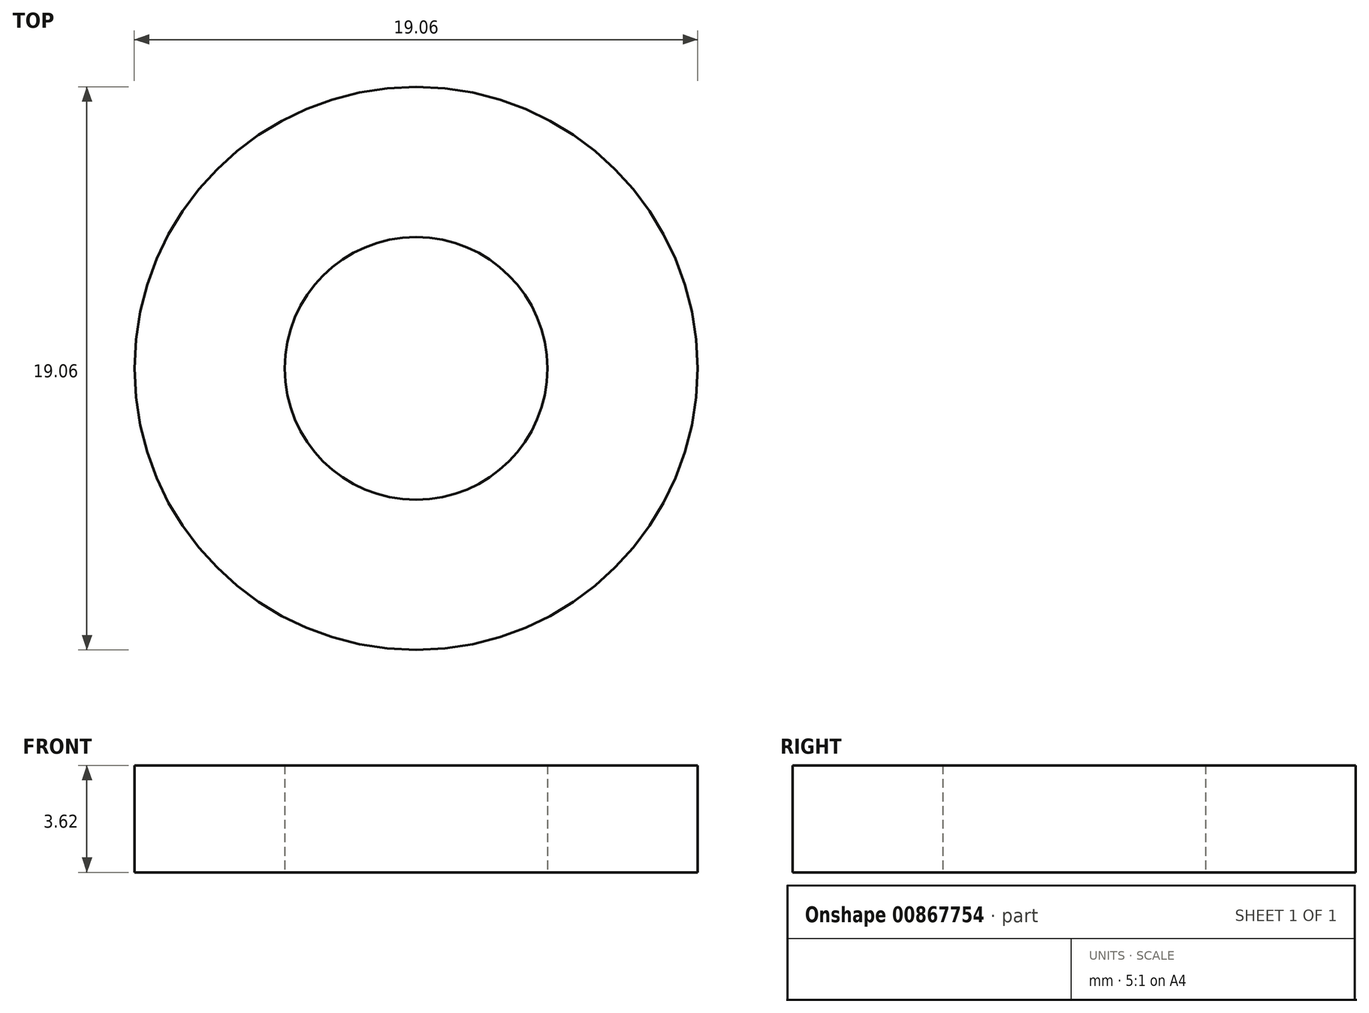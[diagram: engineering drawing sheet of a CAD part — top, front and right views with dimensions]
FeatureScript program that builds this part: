
annotation { "Feature Type Name" : "Feature", "Feature Type Description" : "" }
export const myFeature = defineFeature(function(context is Context, id is Id, definition is map)
    precondition{}
    {
        {
            var Q0;
            Q0=qCreatedBy(makeId("Top.planeOp"),FACE);
            var sketch = newSketch(context, id + "F0", { "sketchPlane" : qUnion([Q0])});
            skCircle(sketch, "E0", {"center": v(0, 0) * mm, "radius": 9.53 * mm});
            skCircle(sketch, "E1", {"center": v(0, 0) * mm, "radius": 4.45 * mm});
            skSolve(sketch);
        }
        {
            var Q0;
            Q0=makeQuery(id+"F0.imprint","IMPRINT",FACE,{"disambiguationData":[TD([[makeQuery(id+"F0.imprint","IMPRINT",EDGE,{"derivedFrom":sQuery(id+"F0.wireOp",EDGE,"E0")}),1.0]])]});
            extrude(context, id + "F1", {"entities" : qUnion([Q0]), "depth" : 3.62 * mm, "offsetDistance" : 25.4 * mm});
        }
    });
